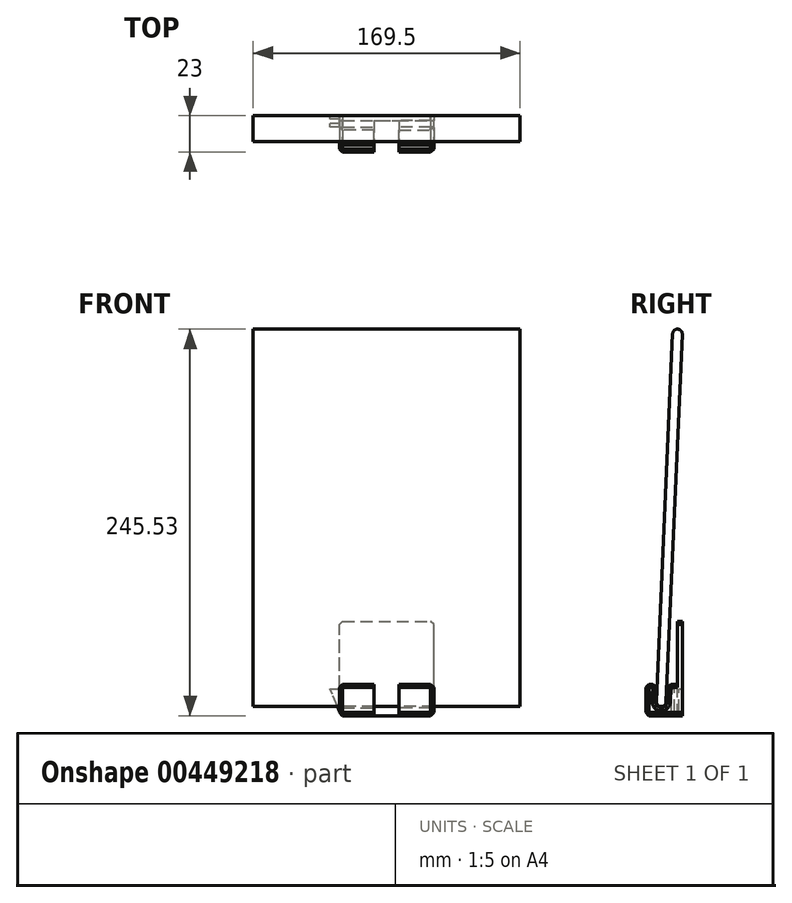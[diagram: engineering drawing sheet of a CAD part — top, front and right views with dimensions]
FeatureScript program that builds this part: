
annotation { "Feature Type Name" : "Feature", "Feature Type Description" : "" }
export const myFeature = defineFeature(function(context is Context, id is Id, definition is map)
    precondition{}
    {
        {
            var Q0;
            Q0=qCreatedBy(makeId("Front.planeOp"),FACE);
            var sketch = newSketch(context, id + "F0", { "sketchPlane" : qUnion([Q0])});
            skLineSegment(sketch, "E0.left", {"start": v(-30, 0) * mm, "end": v(-30, 60) * mm});
            skLineSegment(sketch, "E1", {"start": v(-30, 0) * mm, "end": v(30, 0) * mm});
            skLineSegment(sketch, "E2", {"start": v(30, 0) * mm, "end": v(30, 60) * mm});
            skLineSegment(sketch, "E3", {"start": v(-30, 60) * mm, "end": v(30, 60) * mm});
            skSolve(sketch);
        }
        {
            var Q0;
            Q0=makeQuery(id+"F0.imprint","IMPRINT",FACE,{"disambiguationData":[TD([[makeQuery(id+"F0.imprint","IMPRINT",EDGE,{"derivedFrom":sQuery(id+"F0.wireOp",EDGE,"E0.left")}),-1.0]])]});
            extrude(context, id + "F1", {"entities" : qUnion([Q0]), "depth" : 3 * mm});
        }
        {
            var Q0;
            Q0=qCreatedBy(makeId("Right.planeOp"),FACE);
            var sketch = newSketch(context, id + "F2", { "sketchPlane" : qUnion([Q0])});
            skArc(sketch, "E4", {"start": v(0, 242.34) * mm, "mid": v(-2.92, 245.52) * mm, "end": v(-6.1, 242.6) * mm});
            skArc(sketch, "E5", {"start": v(-16.34, 8.93) * mm, "mid": v(-13.43, 5.75) * mm, "end": v(-10.25, 8.67) * mm});
            skLineSegment(sketch, "E6", {"start": v(0, 242.34) * mm, "end": v(-10.25, 8.67) * mm});
            skLineSegment(sketch, "E7", {"start": v(-6.1, 242.6) * mm, "end": v(-16.34, 8.93) * mm});
            skArc(sketch, "E8", {"start": v(-17.1, 8.97) * mm, "mid": v(-13.46, 5) * mm, "end": v(-9.5, 8.63) * mm});
            skLineSegment(sketch, "E9", {"start": v(-9.5, 8.63) * mm, "end": v(-9, 20) * mm});
            skLineSegment(sketch, "E10", {"start": v(-17.1, 8.97) * mm, "end": v(-16.6, 20) * mm});
            skPoint(sketch, "E11.0", {"position": v(-3, 0) * mm});
            skLineSegment(sketch, "E12", {"start": v(-3, 0) * mm, "end": v(-3, 20) * mm});
            skLineSegment(sketch, "E13", {"start": v(0, 20) * mm, "end": v(-31.15, 20) * mm, "construction": true});
            skPoint(sketch, "E14.orphan", {"position": v(-23, 0) * mm});
            skLineSegment(sketch, "E15", {"start": v(-3, 0) * mm, "end": v(-23, 0) * mm});
            skLineSegment(sketch, "E16", {"start": v(-23, 20) * mm, "end": v(-23, 0) * mm});
            skLineSegment(sketch, "E17", {"start": v(-3, 20) * mm, "end": v(-9, 20) * mm});
            skLineSegment(sketch, "E18", {"start": v(-16.6, 20) * mm, "end": v(-23, 20) * mm});
            skSolve(sketch);
        }
        {
            var Q0;
            Q0=makeQuery(id+"F2.imprint","IMPRINT",FACE,{"disambiguationData":[TD([[makeQuery(id+"F2.imprint","IMPRINT",EDGE,{"derivedFrom":sQuery(id+"F2.wireOp",EDGE,"E8")}),-1.0]])]});
            var Q1;
            Q1=makeQuery(id+"F1.opExtrude","SWEPT_FACE",FACE,{"disambiguationData":[OSD([sQuery(id+"F0.wireOp",EDGE,"E0.left")])]});
            extrude(context, id + "F3", {"entities" : qUnion([Q0]), "endBound" : BoundingType.UP_TO_SURFACE, "oppositeDirection" : true, "endBoundEntityFace" : qUnion([Q1]), "depth" : 23.8 * mm, "hasSecondDirection" : true, "secondDirectionOppositeDirection" : true, "secondDirectionDepth" : 8 * mm});
        }
        {
            var Q0;
            Q0=makeQuery(id+"F3.opExtrude","CAP_EDGE",EDGE,{"disambiguationData":[OSD([sQuery(id+"F2.wireOp",EDGE,"E17")])],"isStart":false});
            var Q1;
            Q1=makeQuery(id+"F3.opExtrude","CAP_EDGE",EDGE,{"disambiguationData":[OSD([sQuery(id+"F2.wireOp",EDGE,"E9")])],"isStart":false});
            var Q2;
            Q2=makeQuery(id+"F3.opExtrude","CAP_EDGE",EDGE,{"disambiguationData":[OSD([sQuery(id+"F2.wireOp",EDGE,"E18")])],"isStart":false});
            var Q3;
            Q3=makeQuery(id+"F3.opExtrude","CAP_EDGE",EDGE,{"disambiguationData":[OSD([sQuery(id+"F2.wireOp",EDGE,"E16")])],"isStart":false});
            var Q4;
            Q4=makeQuery(id+"F3.opExtrude","CAP_EDGE",EDGE,{"disambiguationData":[OSD([sQuery(id+"F2.wireOp",EDGE,"E15")])],"isStart":false});
            var Q5;
            Q5=makeQuery(id+"F1.opExtrude","SWEPT_EDGE",EDGE,{"disambiguationData":[OSD([sQuery(id+"F0.wireOp",EDGE,"E0.left"),sQuery(id+"F0.wireOp",EDGE,"E1")])]});
            var Q6;
            Q6=makeQuery(id+"F1.opExtrude","SWEPT_EDGE",EDGE,{"disambiguationData":[OSD([sQuery(id+"F0.wireOp",EDGE,"E0.left"),sQuery(id+"F0.wireOp",EDGE,"E3")])]});
            var Q7;
            Q7=makeQuery(id+"F1.opExtrude","SWEPT_EDGE",EDGE,{"disambiguationData":[OSD([sQuery(id+"F0.wireOp",EDGE,"E2"),sQuery(id+"F0.wireOp",EDGE,"E3")])]});
            var Q8;
            Q8=makeQuery(id+"F1.opExtrude","SWEPT_EDGE",EDGE,{"disambiguationData":[OSD([sQuery(id+"F0.wireOp",EDGE,"E1"),sQuery(id+"F0.wireOp",EDGE,"E2")])]});
            var Q9;
            Q9=makeQuery(id+"F3.opExtrude","SWEPT_EDGE",EDGE,{"disambiguationData":[OSD([sQuery(id+"F2.wireOp",EDGE,"E9"),sQuery(id+"F2.wireOp",EDGE,"E17")])]});
            var Q10;
            Q10=makeQuery(id+"F3.opExtrude","SWEPT_EDGE",EDGE,{"disambiguationData":[OSD([sQuery(id+"F2.wireOp",EDGE,"E10"),sQuery(id+"F2.wireOp",EDGE,"E18")])]});
            var Q11;
            Q11=makeQuery(id+"F3.opExtrude","SWEPT_EDGE",EDGE,{"disambiguationData":[OSD([sQuery(id+"F2.wireOp",EDGE,"E16"),sQuery(id+"F2.wireOp",EDGE,"E18")])]});
            var Q12;
            Q12=makeQuery(id+"F3.opExtrude","SWEPT_EDGE",EDGE,{"disambiguationData":[OSD([sQuery(id+"F2.wireOp",EDGE,"E15"),sQuery(id+"F2.wireOp",EDGE,"E16")])]});
            chamfer(context, id + "F4", {"entities" : qUnion([Q0, Q1, Q2, Q3, Q4, Q5, Q6, Q7, Q8, Q9, Q10, Q11, Q12]), "width" : 2 * mm, "tangentPropagation" : true});
        }
        {
            var Q0;
            Q0=makeQuery(id+"F3.opExtrude","SWEPT_BODY",BODY,{"disambiguationData":[OSD([sQuery(id+"F2.wireOp",EDGE,"E8"),sQuery(id+"F2.wireOp",EDGE,"E9"),sQuery(id+"F2.wireOp",EDGE,"E10"),sQuery(id+"F2.wireOp",EDGE,"E12"),sQuery(id+"F2.wireOp",EDGE,"E15"),sQuery(id+"F2.wireOp",EDGE,"E16"),sQuery(id+"F2.wireOp",EDGE,"E17"),sQuery(id+"F2.wireOp",EDGE,"E18")])]});
            var Q1;
            Q1=qCreatedBy(makeId("Right.planeOp"),FACE);
            mirror(context, id + "F5", {"operationType" : NewBodyOperationType.ADD, "entities" : qUnion([Q0]), "mirrorPlane" : qUnion([Q1])});
        }
        {
            var Q0;
            Q0=makeQuery(id+"F2.imprint","IMPRINT",FACE,{"disambiguationData":[TD([[makeQuery(id+"F2.imprint","IMPRINT",EDGE,{"derivedFrom":sQuery(id+"F2.wireOp",EDGE,"E4")}),1.0]])]});
            extrude(context, id + "F6", {"entities" : qUnion([Q0]), "endBound" : BoundingType.SYMMETRIC, "depth" : 169.5 * mm});
        }
        {
            var Q0;
            Q0=qCreatedBy(makeId("Front.planeOp"),FACE);
            var sketch = newSketch(context, id + "F7", { "sketchPlane" : qUnion([Q0])});
            skLineSegment(sketch, "E19.0", {"start": v(-30, 2.87) * mm, "end": v(-30, 16.93) * mm});
            skLineSegment(sketch, "E20", {"start": v(-30, 2.87) * mm, "end": v(-36, 16.93) * mm});
            skLineSegment(sketch, "E21", {"start": v(-36, 16.93) * mm, "end": v(-30, 16.93) * mm});
            skPoint(sketch, "E22.orphan", {"position": v(-30, 18) * mm});
            skPoint(sketch, "E23.orphan", {"position": v(-30, 2) * mm});
            skSolve(sketch);
        }
        {
            var Q0;
            Q0 = qSketchRegion(id + "F7", true);
            var Q1;
            Q1=qCreatedBy(id+"FlQUPLxQvXDAW0C_2.planeOp",FACE);
            extrude(context, id + "F8", {"entities" : qUnion([Q0]), "operationType" : NewBodyOperationType.ADD, "endBoundEntityFace" : qUnion([Q1]), "depth" : 7 * mm});
        }
        {
            var Q0;
            Q0 = qSketchRegion(id + "F7", true);
            extrude(context, id + "F9", {"entities" : qUnion([Q0]), "operationType" : NewBodyOperationType.REMOVE, "depth" : (7 - 2) * mm, "hasSecondDirection" : true, "secondDirectionOppositeDirection" : false, "secondDirectionDepth" : 2 * mm});
        }
    });
